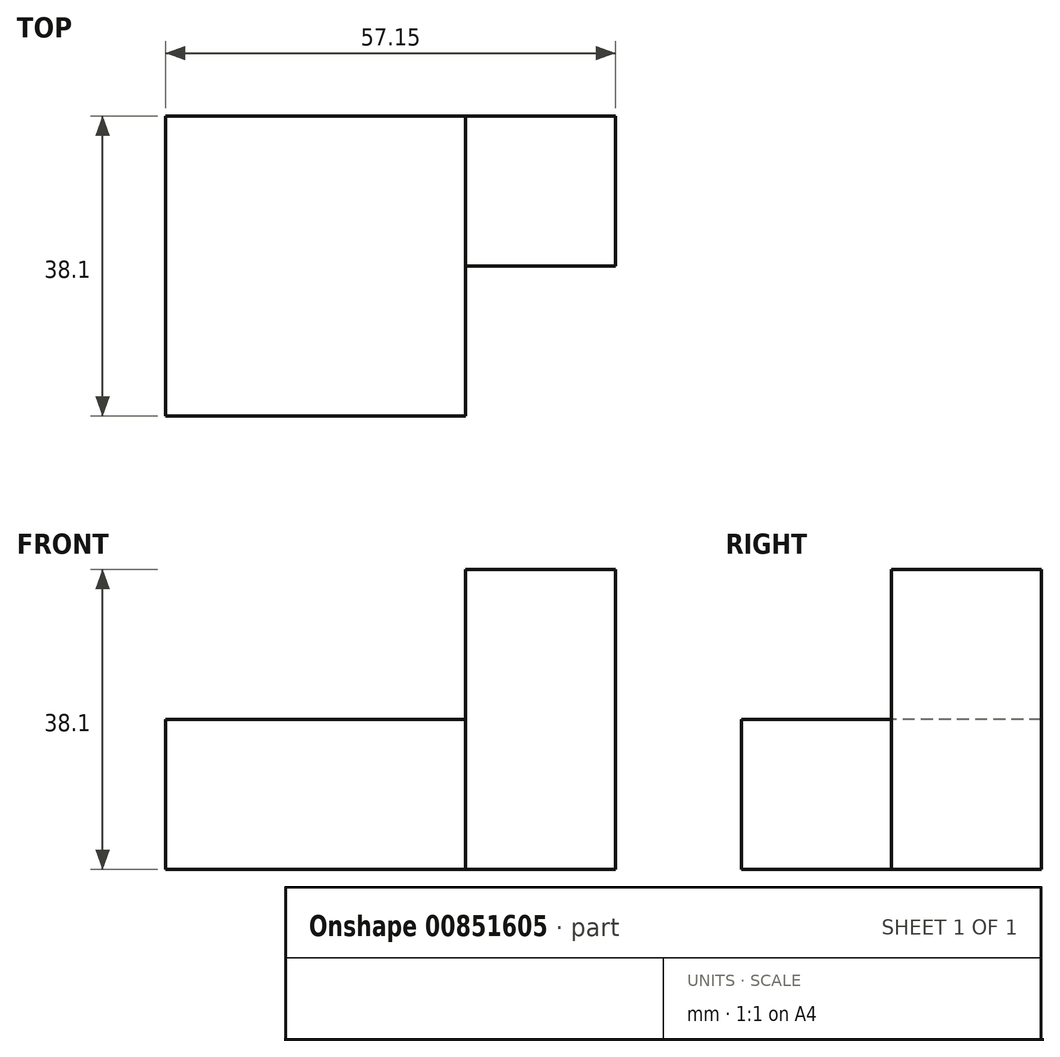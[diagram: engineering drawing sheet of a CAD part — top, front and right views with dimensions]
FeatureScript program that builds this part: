
annotation { "Feature Type Name" : "Feature", "Feature Type Description" : "" }
export const myFeature = defineFeature(function(context is Context, id is Id, definition is map)
    precondition{}
    {
        {
            var Q0;
            Q0=qCreatedBy(makeId("Top.planeOp"),FACE);
            var sketch = newSketch(context, id + "F0", { "sketchPlane" : qUnion([Q0])});
            skLineSegment(sketch, "E0.bottom", {"start": v(19.05, 19.05) * mm, "end": v(-19.05, 19.05) * mm});
            skLineSegment(sketch, "E0.top", {"start": v(19.05, -19.05) * mm, "end": v(-19.05, -19.05) * mm});
            skLineSegment(sketch, "E0.left", {"start": v(19.05, 19.05) * mm, "end": v(19.05, -19.05) * mm});
            skLineSegment(sketch, "E0.right", {"start": v(-19.05, 19.05) * mm, "end": v(-19.05, -19.05) * mm});
            skPoint(sketch, "E0.middle", {"position": v(0, 0) * mm});
            skLineSegment(sketch, "E1", {"start": v(19.05, 19.05) * mm, "end": v(38.1, 19.05) * mm});
            skLineSegment(sketch, "E2", {"start": v(38.1, 19.05) * mm, "end": v(38.1, 0) * mm});
            skLineSegment(sketch, "E3", {"start": v(38.1, 0) * mm, "end": v(19.05, 0) * mm});
            skSolve(sketch);
        }
        {
            var Q0;
            {var subQ0=sQuery(id+"F0.wireOp",EDGE,"E1");Q0=makeQuery(id+"F0.imprint","IMPRINT",FACE,{"disambiguationData":[TD([[makeQuery(id+"F0.imprint","IMPRINT",EDGE,{"derivedFrom":subQ0}),-1.0]])]});}
            extrude(context, id + "F1", {"entities" : qUnion([Q0]), "depth" : 38.1 * mm, "offsetDistance" : 25.4 * mm});
        }
        {
            var Q0;
            {var subQ3=sQuery(id+"F0.wireOp",EDGE,"E0.bottom");Q0=makeQuery(id+"F0.imprint","IMPRINT",FACE,{"disambiguationData":[TD([[makeQuery(id+"F0.imprint","IMPRINT",EDGE,{"derivedFrom":subQ3}),1.0]])]});}
            extrude(context, id + "F2", {"entities" : qUnion([Q0]), "operationType" : NewBodyOperationType.ADD, "depth" : 19.05 * mm, "offsetDistance" : 25.4 * mm});
        }
    });
